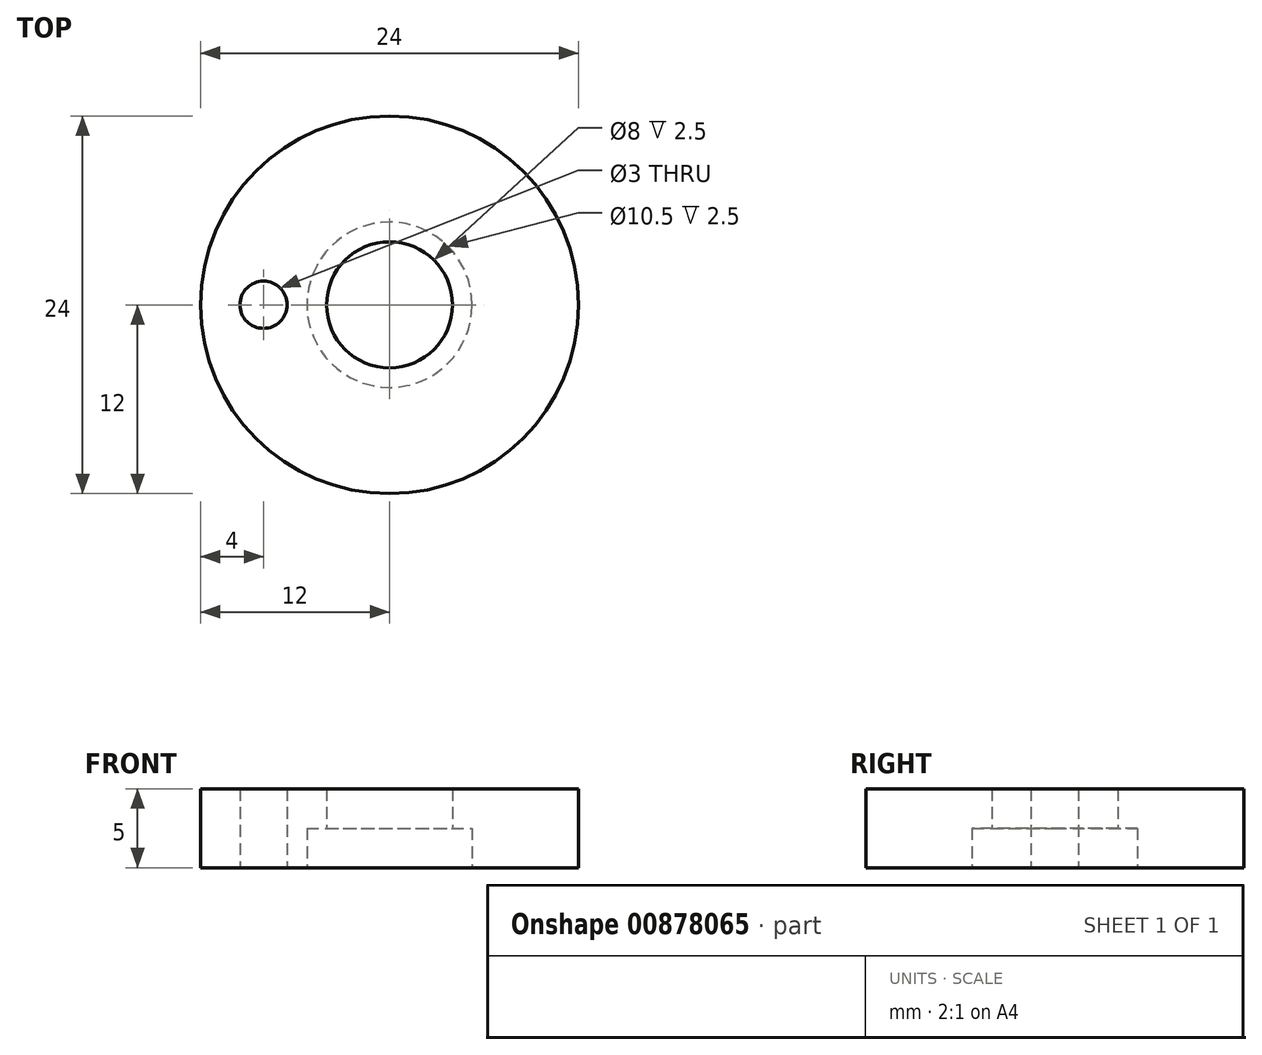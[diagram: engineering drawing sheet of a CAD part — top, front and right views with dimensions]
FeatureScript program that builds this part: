
annotation { "Feature Type Name" : "Feature", "Feature Type Description" : "" }
export const myFeature = defineFeature(function(context is Context, id is Id, definition is map)
    precondition{}
    {
        {
            var Q0;
            Q0=qCreatedBy(makeId("Top.planeOp"),FACE);
            var sketch = newSketch(context, id + "F0", { "sketchPlane" : qUnion([Q0])});
            skCircle(sketch, "E0", {"center": v(0, 0) * mm, "radius": 12 * mm});
            skSolve(sketch);
        }
        {
            var Q0;
            Q0=makeQuery(id+"F0.imprint","IMPRINT",FACE,{"disambiguationData":[TD([[makeQuery(id+"F0.imprint","IMPRINT",EDGE,{"derivedFrom":sQuery(id+"F0.wireOp",EDGE,"E0")}),1.0]])]});
            extrude(context, id + "F1", {"entities" : qUnion([Q0]), "depth" : 5 * mm, "offsetDistance" : 25 * mm});
        }
        {
            var Q0;
            Q0=makeQuery(id+"F1.opExtrude","CAP_FACE",FACE,{"disambiguationData":[OSD([sQuery(id+"F0.wireOp",EDGE,"E0")])],"isStart":true});
            var sketch = newSketch(context, id + "F2", { "sketchPlane" : qUnion([Q0])});
            skCircle(sketch, "E1", {"center": v(0, 0) * mm, "radius": 4 * mm});
            skSolve(sketch);
        }
        {
            var Q0;
            Q0=makeQuery(id+"F2.imprint","IMPRINT",FACE,{"disambiguationData":[TD([[makeQuery(id+"F2.imprint","IMPRINT",EDGE,{"derivedFrom":sQuery(id+"F2.wireOp",EDGE,"E1")}),1.0]])]});
            extrude(context, id + "F3", {"entities" : qUnion([Q0]), "operationType" : NewBodyOperationType.REMOVE, "endBound" : BoundingType.UP_TO_NEXT, "oppositeDirection" : true, "depth" : 25 * mm, "offsetDistance" : 25 * mm});
        }
        {
            var Q0;
            Q0=makeQuery(id+"F1.opExtrude","CAP_FACE",FACE,{"disambiguationData":[OSD([sQuery(id+"F0.wireOp",EDGE,"E0")])],"isStart":true});
            var sketch = newSketch(context, id + "F4", { "sketchPlane" : qUnion([Q0])});
            skCircle(sketch, "E2", {"center": v(0, 0) * mm, "radius": 5.25 * mm});
            skSolve(sketch);
        }
        {
            var Q0;
            Q0=makeQuery(id+"F1.opExtrude","CAP_FACE",FACE,{"disambiguationData":[OSD([sQuery(id+"F0.wireOp",EDGE,"E0")])],"isStart":true});
            var sketch = newSketch(context, id + "F5", { "sketchPlane" : qUnion([Q0])});
            skCircle(sketch, "E3", {"center": v(-8, 0) * mm, "radius": 1.5 * mm});
            skSolve(sketch);
        }
        {
            var Q0;
            Q0=makeQuery(id+"F5.imprint","IMPRINT",FACE,{"disambiguationData":[TD([[makeQuery(id+"F5.imprint","IMPRINT",EDGE,{"derivedFrom":sQuery(id+"F5.wireOp",EDGE,"E3")}),1.0]])]});
            extrude(context, id + "F6", {"entities" : qUnion([Q0]), "operationType" : NewBodyOperationType.REMOVE, "endBound" : BoundingType.UP_TO_NEXT, "oppositeDirection" : true, "depth" : 25 * mm, "offsetDistance" : 25 * mm});
        }
        {
            var Q0;
            Q0 = qSketchRegion(id + "F4", true);
            extrude(context, id + "F7", {"entities" : qUnion([Q0]), "operationType" : NewBodyOperationType.REMOVE, "oppositeDirection" : true, "depth" : 2.5 * mm, "offsetDistance" : 25 * mm});
        }
    });
